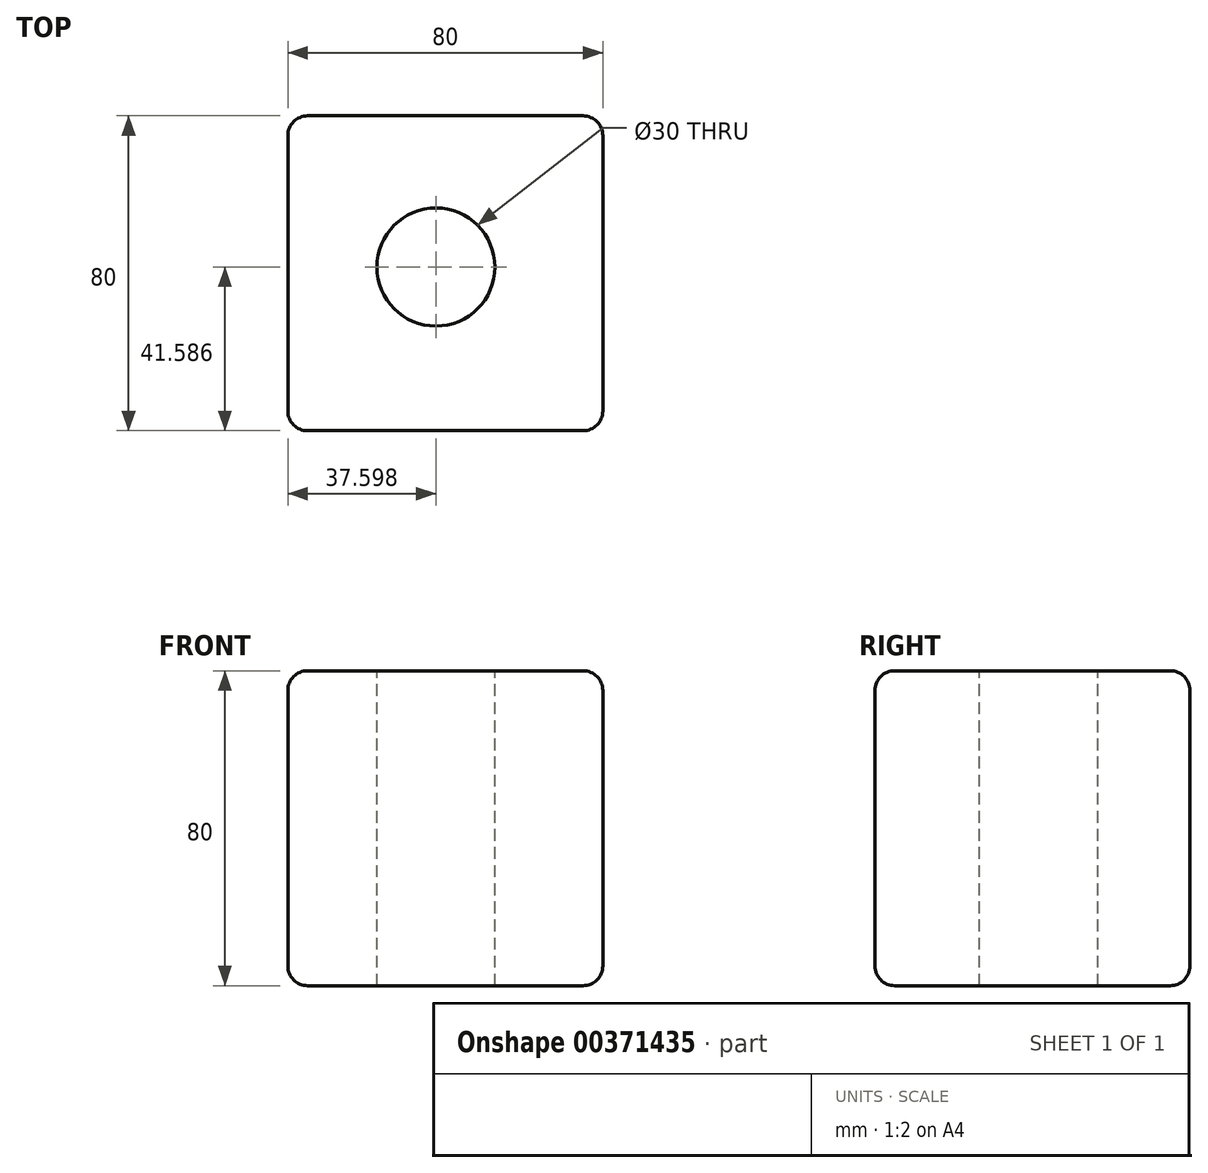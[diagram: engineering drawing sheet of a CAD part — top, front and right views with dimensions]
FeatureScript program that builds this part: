
annotation { "Feature Type Name" : "Feature", "Feature Type Description" : "" }
export const myFeature = defineFeature(function(context is Context, id is Id, definition is map)
    precondition{}
    {
        {
            var Q0;
            Q0=qCreatedBy(makeId("Top.planeOp"),FACE);
            var sketch = newSketch(context, id + "F0", { "sketchPlane" : qUnion([Q0])});
            skLineSegment(sketch, "E0.bottom", {"start": v(-31.65, 50.44) * mm, "end": v(48.35, 50.44) * mm});
            skLineSegment(sketch, "E0.top", {"start": v(-31.65, -29.56) * mm, "end": v(48.35, -29.56) * mm});
            skLineSegment(sketch, "E0.left", {"start": v(-31.65, 50.44) * mm, "end": v(-31.65, -29.56) * mm});
            skLineSegment(sketch, "E0.right", {"start": v(48.35, 50.44) * mm, "end": v(48.35, -29.56) * mm});
            skSolve(sketch);
        }
        {
            var Q0;
            Q0=makeQuery(id+"F0.imprint","IMPRINT",FACE,{"disambiguationData":[TD([[makeQuery(id+"F0.imprint","IMPRINT",EDGE,{"derivedFrom":sQuery(id+"F0.wireOp",EDGE,"E0.bottom")}),-1.0]])]});
            extrude(context, id + "F1", {"entities" : qUnion([Q0]), "endBound" : BoundingType.SYMMETRIC, "depth" : 80 * mm});
        }
        {
            var Q0;
            Q0=makeQuery(id+"F1.opExtrude","CAP_FACE",FACE,{"disambiguationData":[OSD([sQuery(id+"F0.wireOp",EDGE,"E0.bottom"),sQuery(id+"F0.wireOp",EDGE,"E0.top"),sQuery(id+"F0.wireOp",EDGE,"E0.left"),sQuery(id+"F0.wireOp",EDGE,"E0.right")])],"isStart":false});
            var sketch = newSketch(context, id + "F2", { "sketchPlane" : qUnion([Q0])});
            skCircle(sketch, "E1", {"center": v(5.95, 12.03) * mm, "radius": 15 * mm});
            skSolve(sketch);
        }
        {
            var Q0;
            Q0=makeQuery(id+"F2.imprint","IMPRINT",FACE,{"disambiguationData":[TD([[makeQuery(id+"F2.imprint","IMPRINT",EDGE,{"derivedFrom":sQuery(id+"F2.wireOp",EDGE,"E1")}),1.0]])]});
            extrude(context, id + "F3", {"entities" : qUnion([Q0]), "operationType" : NewBodyOperationType.REMOVE, "endBound" : BoundingType.THROUGH_ALL, "oppositeDirection" : true, "depth" : 25 * mm});
        }
        {
            var Q0;
            Q0=makeQuery(id+"F1.opExtrude","CAP_EDGE",EDGE,{"disambiguationData":[OSD([sQuery(id+"F0.wireOp",EDGE,"E0.bottom")])],"isStart":true});
            var Q1;
            Q1=makeQuery(id+"F1.opExtrude","CAP_EDGE",EDGE,{"disambiguationData":[OSD([sQuery(id+"F0.wireOp",EDGE,"E0.right")])],"isStart":true});
            var Q2;
            Q2=makeQuery(id+"F1.opExtrude","CAP_EDGE",EDGE,{"disambiguationData":[OSD([sQuery(id+"F0.wireOp",EDGE,"E0.left")])],"isStart":true});
            var Q3;
            Q3=makeQuery(id+"F1.opExtrude","CAP_EDGE",EDGE,{"disambiguationData":[OSD([sQuery(id+"F0.wireOp",EDGE,"E0.top")])],"isStart":true});
            var Q4;
            Q4=makeQuery(id+"F1.opExtrude","SWEPT_EDGE",EDGE,{"disambiguationData":[OSD([sQuery(id+"F0.wireOp",EDGE,"E0.bottom"),sQuery(id+"F0.wireOp",EDGE,"E0.right")])]});
            var Q5;
            Q5=makeQuery(id+"F1.opExtrude","CAP_EDGE",EDGE,{"disambiguationData":[OSD([sQuery(id+"F0.wireOp",EDGE,"E0.right")])],"isStart":false});
            var Q6;
            Q6=makeQuery(id+"F1.opExtrude","SWEPT_EDGE",EDGE,{"disambiguationData":[OSD([sQuery(id+"F0.wireOp",EDGE,"E0.top"),sQuery(id+"F0.wireOp",EDGE,"E0.right")])]});
            var Q7;
            Q7=makeQuery(id+"F1.opExtrude","SWEPT_EDGE",EDGE,{"disambiguationData":[OSD([sQuery(id+"F0.wireOp",EDGE,"E0.bottom"),sQuery(id+"F0.wireOp",EDGE,"E0.left")])]});
            var Q8;
            Q8=makeQuery(id+"F1.opExtrude","CAP_EDGE",EDGE,{"disambiguationData":[OSD([sQuery(id+"F0.wireOp",EDGE,"E0.bottom")])],"isStart":false});
            var Q9;
            Q9=makeQuery(id+"F1.opExtrude","CAP_EDGE",EDGE,{"disambiguationData":[OSD([sQuery(id+"F0.wireOp",EDGE,"E0.left")])],"isStart":false});
            var Q10;
            Q10=makeQuery(id+"F1.opExtrude","SWEPT_EDGE",EDGE,{"disambiguationData":[OSD([sQuery(id+"F0.wireOp",EDGE,"E0.top"),sQuery(id+"F0.wireOp",EDGE,"E0.left")])]});
            var Q11;
            Q11=makeQuery(id+"F1.opExtrude","CAP_EDGE",EDGE,{"disambiguationData":[OSD([sQuery(id+"F0.wireOp",EDGE,"E0.top")])],"isStart":false});
            fillet(context, id + "F4", {"entities" : qUnion([Q0, Q1, Q2, Q3, Q4, Q5, Q6, Q7, Q8, Q9, Q10, Q11]), "radius" : 5 * mm, "tangentPropagation" : true, "allowEdgeOverflow" : false});
        }
    });
